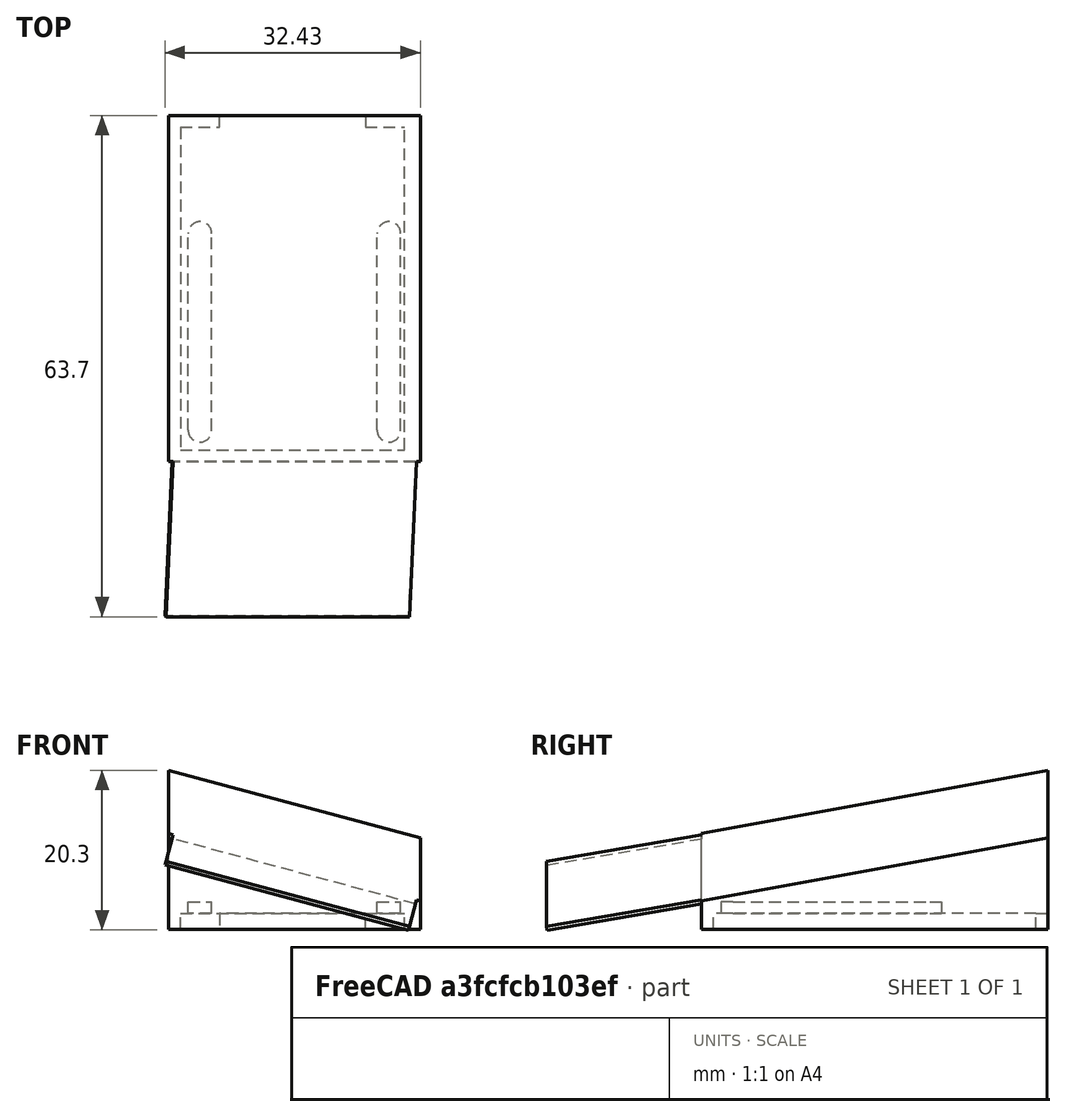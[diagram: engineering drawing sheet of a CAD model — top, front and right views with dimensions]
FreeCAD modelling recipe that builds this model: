
FCSTD DOCUMENT  (FreeCAD 0.18RUnknown)
Label: cam-holder3
License: All rights reserved
LicenseURL: http://en.wikipedia.org/wiki/All_rights_reserved
objects: Sketcher::SketchObject×4, PartDesign::Pad×2, PartDesign::Pocket×2, PartDesign::Plane×1, PartDesign::Body×1, Mesh::Feature×1
note: 14 computed .brp shape members not serialized (recipe doc carries the construction recipe); baked Part::Feature solids carry a one-line shape summary decoded from their .brp

FEATURE [Sketcher::SketchObject] Sketch
  MapMode = 5
  Support = -> [XY_Plane]
  sketch-geometry (4):
    g0: LineSegment StartX=0 StartY=0 StartZ=0 EndX=32 EndY=0 EndZ=0
    g1: LineSegment StartX=32 StartY=0 StartZ=0 EndX=32 EndY=44 EndZ=0
    g2: LineSegment StartX=32 StartY=44 StartZ=0 EndX=0 EndY=44 EndZ=0
    g3: LineSegment StartX=0 StartY=44 StartZ=0 EndX=0 EndY=0 EndZ=0
  constraints (11):
    c: Coincident(g0,g1)
    c: Coincident(g1,g2)
    c: Coincident(g2,g3)
    c: Coincident(g3,g0)
    c: Horizontal(g0)
    c: Horizontal(g2)
    c: Vertical(g1)
    c: Vertical(g3)
    c: Coincident(g0,g-1)
    c: Distance(g2) = 32
    c: Distance(g3) = 44
FEATURE [PartDesign::Plane] DatumPlane
  AttachmentOffset = pos=(0.6,0,12) rot=(0.552011,0.830664,-0.072674;0.314367rad)
  Length = 59.9961
  MapMode = 2
  Placement = pos=(0.6,0,12) rot=(0.552011,0.830664,-0.072674;0.314367rad)
  ResizeMode = 0
  Support = -> [Sketch]
  Width = 81.2931
FEATURE [PartDesign::Pad] Pad
  Length = 10
  Length2 = 100
  Profile = -> Sketch
  Type = 3
  UpToFace = -> DatumPlane [Plane]
FEATURE [Sketcher::SketchObject] Sketch001
  MapMode = 5
  Placement = pos=(0,0,0) rot=(1,0,0;3.14159rad)
  Support = -> [Pad]
  sketch-geometry (8):
    g0: LineSegment StartX=1.5 StartY=-1.5 StartZ=0 EndX=30 EndY=-1.5 EndZ=0
    g1: LineSegment StartX=30 StartY=-1.5 StartZ=0 EndX=30 EndY=-42.5 EndZ=0
    g2: LineSegment StartX=1.5 StartY=-42.5 StartZ=0 EndX=1.5 EndY=-1.5 EndZ=0
    g3: LineSegment StartX=1.5 StartY=-42.5 StartZ=0 EndX=6.5 EndY=-42.5 EndZ=0
    g4: LineSegment StartX=6.5 StartY=-42.5 StartZ=0 EndX=6.5 EndY=-47.5 EndZ=0
    g5: LineSegment StartX=6.5 StartY=-47.5 StartZ=0 EndX=25 EndY=-47.5 EndZ=0
    g6: LineSegment StartX=25 StartY=-47.5 StartZ=0 EndX=25 EndY=-42.5 EndZ=0
    g7: LineSegment StartX=25 StartY=-42.5 StartZ=0 EndX=30 EndY=-42.5 EndZ=0
  constraints (24):
    c: Coincident(g0,g1)
    c: Coincident(g2,g0)
    c: Horizontal(g0)
    c: Vertical(g1)
    c: Vertical(g2)
    c: Distance(g0) = 28.5
    c: Distance(g2) = 41
    c: Distance(g-1,g0) = 1.5
    c: Distance(g-1,g2) = 1.5
    c: Coincident(g3,g4)
    c: Coincident(g4,g5)
    c: Coincident(g5,g6)
    c: Coincident(g6,g7)
    c: Coincident(g3,g2)
    c: Coincident(g7,g1)
    c: Horizontal(g3)
    c: Horizontal(g7)
    c: Horizontal(g5)
    c: Vertical(g4)
    c: Vertical(g6)
    c: Distance(g3) = 5
    c: Equal(g3,g7)
    c: Equal(g4,g3)
    c: Equal(g4,g6)
FEATURE [PartDesign::Pocket] Pocket
  BaseFeature = -> Pad
  Length = 2
  Length2 = 100
  Profile = -> Sketch001
  Type = 0
FEATURE [Sketcher::SketchObject] Sketch002
  ExternalGeometry = -> [Pocket]
  MapMode = 5
  Placement = pos=(0.6,0,12) rot=(0.552011,0.830664,-0.072674;0.314367rad)
  Support = -> [DatumPlane]
  sketch-geometry (4):
    g0: LineSegment StartX=-0.621166 StartY=0 StartZ=0 EndX=32.5077 EndY=2.2e-15 EndZ=0
    g1: LineSegment StartX=32.5077 StartY=2.2e-15 StartZ=0 EndX=32.5077 EndY=-20 EndZ=0
    g2: LineSegment StartX=32.5077 StartY=-20 StartZ=0 EndX=-0.621166 EndY=-20 EndZ=0
    g3: LineSegment StartX=-0.621166 StartY=-20 StartZ=0 EndX=-0.621166 EndY=0 EndZ=0
  constraints (10):
    c: Coincident(g0,g1)
    c: Coincident(g1,g2)
    c: Coincident(g2,g3)
    c: Coincident(g3,g0)
    c: Horizontal(g2)
    c: Vertical(g1)
    c: Vertical(g3)
    c: Coincident(g0,g-3)
    c: Coincident(g-4,g0)
    c: Distance(g1) = 20
FEATURE [PartDesign::Pad] Pad001
  BaseFeature = -> Pocket
  Length = 0.5
  Length2 = 0.5
  Offset = 0.5
  Profile = -> Sketch002
  Type = 0
  expr: Length = 0.5
FEATURE [Sketcher::SketchObject] Sketch003
  ExternalGeometry = -> [Pad001]
  MapMode = 5
  Placement = pos=(0,0,2) rot=(1,0,0;3.14159rad)
  Support = -> [Pad001]
  sketch-geometry (12):
    g0: ArcOfCircle CenterX=4 CenterY=-4 CenterZ=0 NormalX=0 NormalY=0 NormalZ=1 AngleXU=0 Radius=1.5 StartAngle=0 EndAngle=3.14159
    g1: ArcOfCircle CenterX=4 CenterY=-29 CenterZ=0 NormalX=0 NormalY=0 NormalZ=1 AngleXU=0 Radius=1.5 StartAngle=3.14159 EndAngle=6.28319
    g2: LineSegment StartX=2.5 StartY=-4 StartZ=0 EndX=2.5 EndY=-29 EndZ=0
    g3: LineSegment StartX=5.5 StartY=-4 StartZ=0 EndX=5.5 EndY=-29 EndZ=0
    g4: ArcOfCircle CenterX=28 CenterY=-4 CenterZ=0 NormalX=0 NormalY=0 NormalZ=1 AngleXU=0 Radius=1.5 StartAngle=-3.2e-14 EndAngle=3.14159
    g5: ArcOfCircle CenterX=28 CenterY=-29 CenterZ=0 NormalX=0 NormalY=0 NormalZ=1 AngleXU=0 Radius=1.5 StartAngle=3.14159 EndAngle=6.28319
    g6: LineSegment StartX=26.5 StartY=-4 StartZ=0 EndX=26.5 EndY=-29 EndZ=0
    g7: LineSegment StartX=29.5 StartY=-4 StartZ=0 EndX=29.5 EndY=-29 EndZ=0
    g8: LineSegment [constr] StartX=4 StartY=-4 StartZ=0 EndX=28 EndY=-4 EndZ=0
    g9: LineSegment [constr] StartX=4 StartY=-29 StartZ=0 EndX=28 EndY=-29 EndZ=0
    g10: LineSegment [constr] StartX=2.5 StartY=-4 StartZ=0 EndX=5.5 EndY=-4 EndZ=0
    g11: LineSegment [constr] StartX=26.5 StartY=-4 StartZ=0 EndX=29.5 EndY=-4 EndZ=0
  constraints (31):
    c: Tangent(g0,g3) = 1.5708
    c: Tangent(g0,g2) = -1.5708
    c: Tangent(g2,g1) = -1.5708
    c: Tangent(g3,g1) = 1.5708
    c: Vertical(g2)
    c: Equal(g0,g1)
    c: Tangent(g4,g7) = 1.5708
    c: Tangent(g4,g6) = -1.5708
    c: Tangent(g6,g5) = -1.5708
    c: Tangent(g7,g5) = 1.5708
    c: Vertical(g6)
    c: Coincident(g8,g4)
    c: Coincident(g9,g5)
    c: Coincident(g9,g1)
    c: Horizontal(g8)
    c: Horizontal(g9)
    c: PointOnObject(g10,g3)
    c: PointOnObject(g11,g7)
    c: Horizontal(g10)
    c: Horizontal(g11)
    c: Equal(g10,g11)
    c: Equal(g8,g9)
    c: Coincident(g10,g0)
    c: Coincident(g11,g4)
    c: Distance(g-1,g8) = 4
    c: Coincident(g0,g8)
    c: Distance(g-1,g2) = 2.5
    c: Equal(g10,g11)
    c: Distance(g10) = 3
    c: Distance(g4,g-3) = 2.5
    c: Distance(g3) = 25
FEATURE [PartDesign::Pocket] Pocket001
  BaseFeature = -> Pad001
  Length = 1.5
  Length2 = 100
  Profile = -> Sketch003
  Type = 0
FEATURE [PartDesign::Body] Body
  Group = -> [Sketch,DatumPlane,Pad,Sketch001,Pocket,Sketch002,Pad001,Sketch003,Pocket001]
  Origin = -> Origin
  Tip = -> Pocket001
FEATURE [Mesh::Feature] Mesh  label="Pocket001 (Meshed)"
